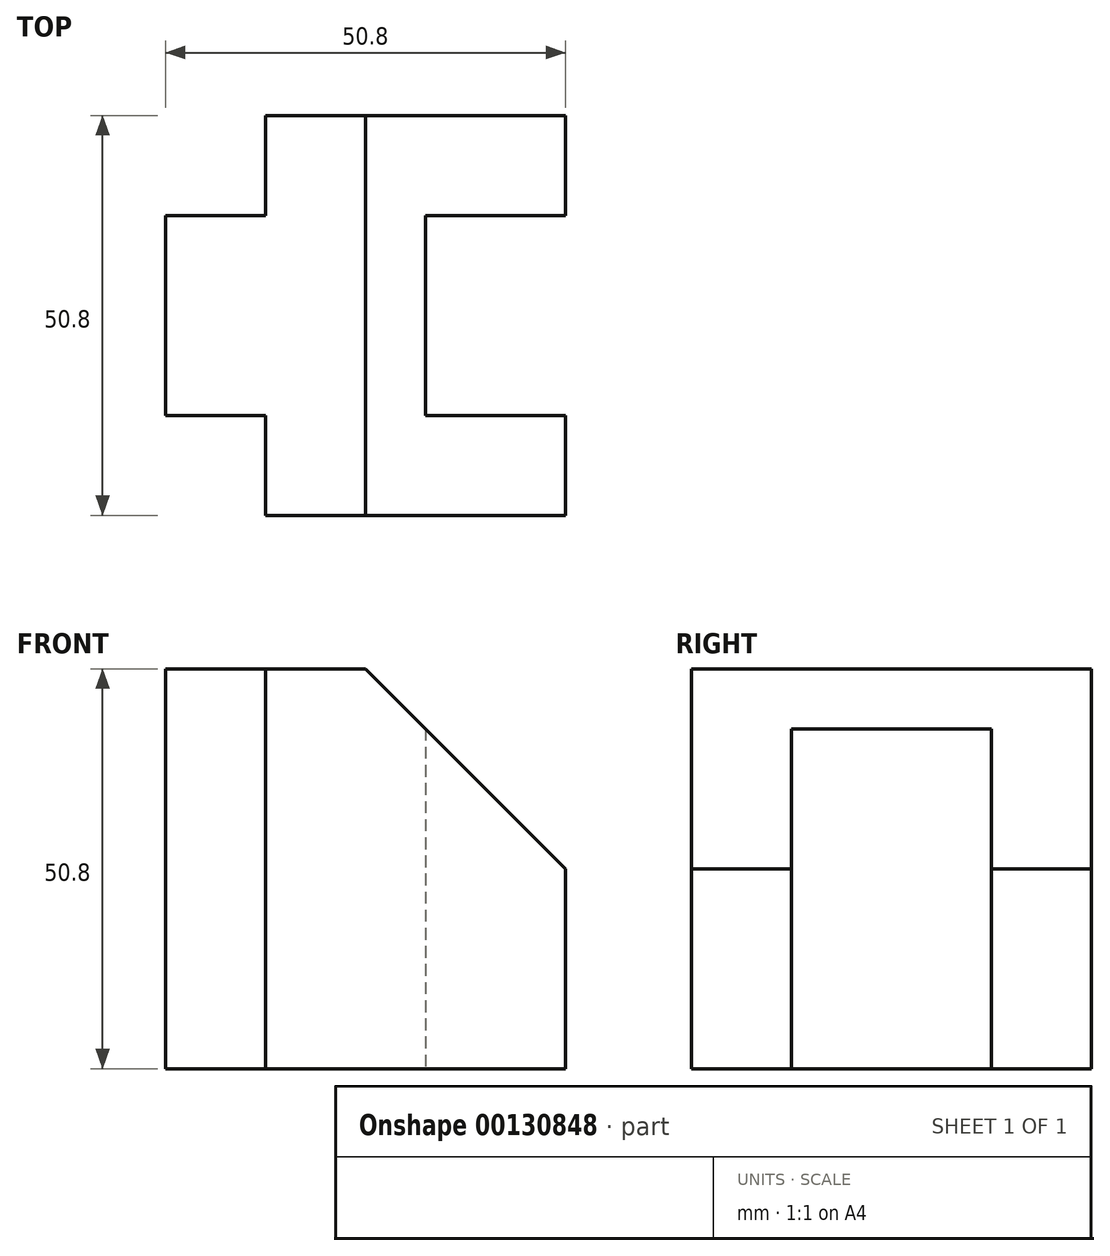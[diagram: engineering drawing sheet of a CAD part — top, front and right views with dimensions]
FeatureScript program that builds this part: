
annotation { "Feature Type Name" : "Feature", "Feature Type Description" : "" }
export const myFeature = defineFeature(function(context is Context, id is Id, definition is map)
    precondition{}
    {
        {
            var Q0;
            Q0=qCreatedBy(makeId("Top.planeOp"),FACE);
            var sketch = newSketch(context, id + "F0", { "sketchPlane" : qUnion([Q0])});
            skLineSegment(sketch, "E0", {"start": v(17.78, -25.4) * mm, "end": v(-20.32, -25.4) * mm});
            skLineSegment(sketch, "E1", {"start": v(-20.32, -25.4) * mm, "end": v(-20.32, -12.7) * mm});
            skLineSegment(sketch, "E2", {"start": v(-20.32, -12.7) * mm, "end": v(-33.02, -12.7) * mm});
            skLineSegment(sketch, "E3", {"start": v(-33.02, -12.7) * mm, "end": v(-33.02, 0) * mm});
            skLineSegment(sketch, "E4", {"start": v(-33.02, 0) * mm, "end": v(-33.02, 12.7) * mm});
            skLineSegment(sketch, "E5", {"start": v(-33.02, 12.7) * mm, "end": v(-20.32, 12.7) * mm});
            skLineSegment(sketch, "E6", {"start": v(-20.32, 12.7) * mm, "end": v(-20.32, 25.4) * mm});
            skLineSegment(sketch, "E7", {"start": v(-20.32, 25.4) * mm, "end": v(17.78, 25.4) * mm});
            skLineSegment(sketch, "E8", {"start": v(17.78, 25.4) * mm, "end": v(17.78, 12.7) * mm});
            skLineSegment(sketch, "E9", {"start": v(17.78, 12.7) * mm, "end": v(0, 12.7) * mm});
            skLineSegment(sketch, "E10", {"start": v(0, 12.7) * mm, "end": v(0, -12.7) * mm});
            skLineSegment(sketch, "E11", {"start": v(0, -12.7) * mm, "end": v(17.78, -12.7) * mm});
            skLineSegment(sketch, "E12", {"start": v(17.78, -12.7) * mm, "end": v(17.78, -25.4) * mm});
            skSolve(sketch);
        }
        {
            var Q0;
            Q0 = qSketchRegion(id + "F0", true);
            extrude(context, id + "F1", {"entities" : qUnion([Q0]), "depth" : 50.8 * mm});
        }
        {
            var Q0;
            Q0=makeQuery(id+"F1.opExtrude","SWEPT_FACE",FACE,{"disambiguationData":[OSD([sQuery(id+"F0.wireOp",EDGE,"E0")])]});
            var sketch = newSketch(context, id + "F2", { "sketchPlane" : qUnion([Q0])});
            skLineSegment(sketch, "E13", {"start": v(-7.62, 50.8) * mm, "end": v(17.78, 25.4) * mm});
            skLineSegment(sketch, "E14", {"start": v(17.78, 25.4) * mm, "end": v(17.78, 50.8) * mm});
            skLineSegment(sketch, "E15", {"start": v(17.78, 50.8) * mm, "end": v(-7.62, 50.8) * mm});
            skSolve(sketch);
        }
        {
            var Q0;
            Q0 = qSketchRegion(id + "F2", true);
            extrude(context, id + "F3", {"entities" : qUnion([Q0]), "operationType" : NewBodyOperationType.REMOVE, "endBound" : BoundingType.THROUGH_ALL, "oppositeDirection" : true, "depth" : 25.4 * mm});
        }
    });
